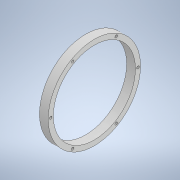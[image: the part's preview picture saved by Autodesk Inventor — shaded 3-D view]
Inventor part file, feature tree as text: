
AUTODESK INVENTOR PART (.ipt)
format: ipt  version: 2020 (Build 240168000, 168)  size: 146,944 bytes
history: native  units: mm
features: sketch x2, revolve x1, hole x1, pattern_circular x1, projected_geometry x1
ambient origin geometry x8: Origin, YZ Plane, XZ Plane, XY Plane, X Axis, Y Axis, Z Axis, Center Point
bodies: Solid1 (feature_tree)
feature tree (6):
  revolve  "Revolution1"  [1 undecoded]
  hole  "Hole1"  [1 undecoded]
  pattern_circular  "Circular Pattern1"  [2 undecoded]
  sketch  "Sketch1"  dims[d11=90.0deg d30=15.4mm]
  sketch  "Sketch2"  dims[d31=9.0mm d33=4.5mm d34=4.5mm d35=4.5mm d36=8.0mm d37=9.4mm d38=2.0mm d39=90.0deg d40=8.0mm d41=20.594885mm d42=60.0mm d43=360.0deg d47=72.5mm]
  projected_geometry  "Projected Loop1"
note: 4 required parameter values undecoded (feature->parameter linkage not recoverable at this tier; creation-order binding heuristic only, values carry confidence <= 0.55)